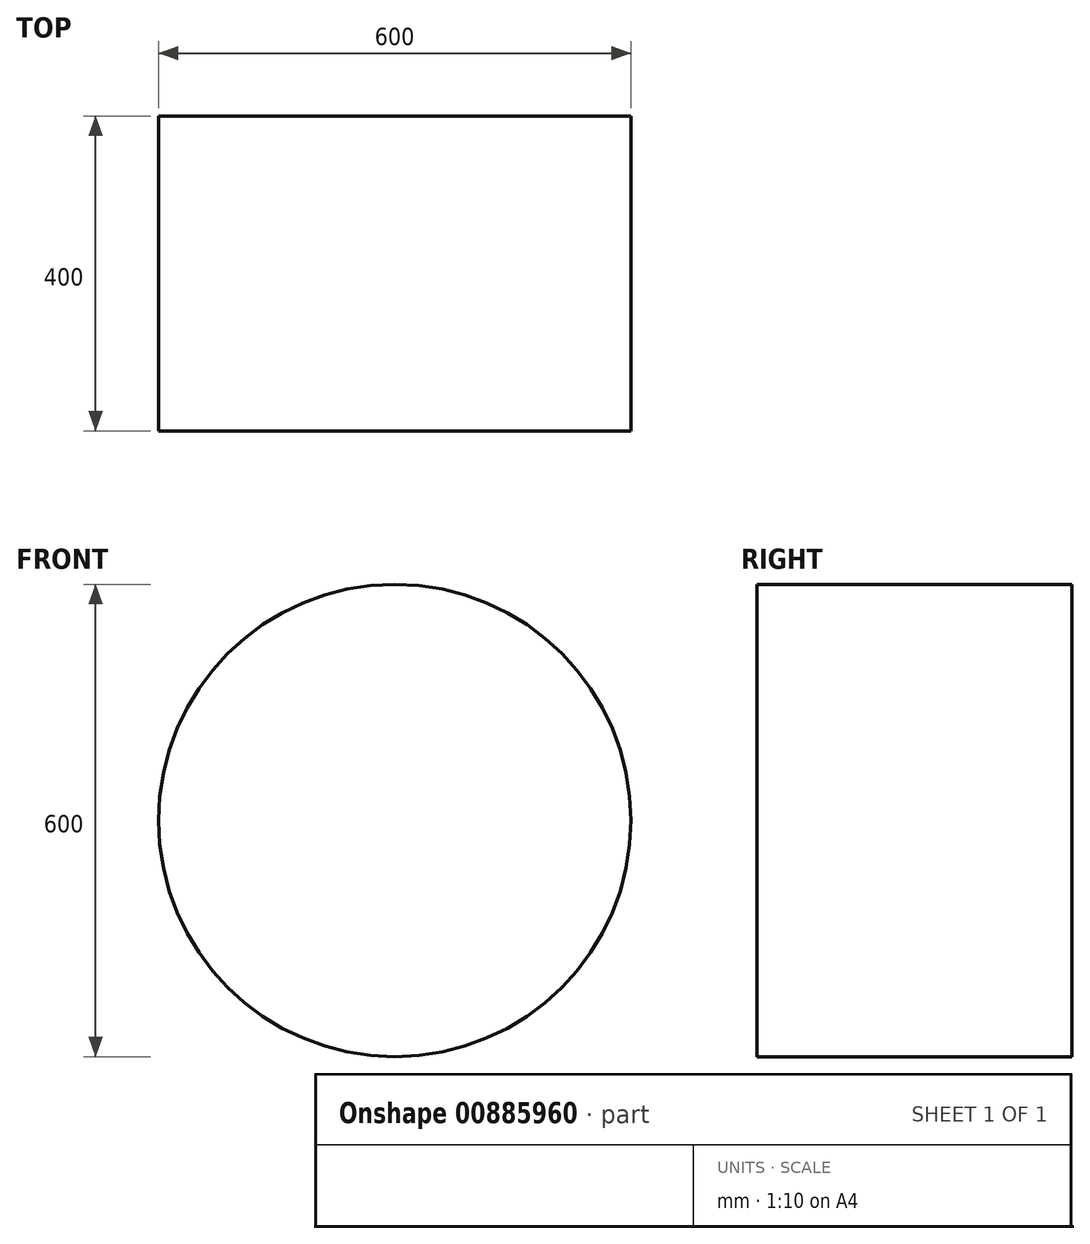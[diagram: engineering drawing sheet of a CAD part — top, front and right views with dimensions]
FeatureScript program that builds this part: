
annotation { "Feature Type Name" : "Feature", "Feature Type Description" : "" }
export const myFeature = defineFeature(function(context is Context, id is Id, definition is map)
    precondition{}
    {
        {
            var Q0;
            Q0=qCreatedBy(makeId("Front.planeOp"),FACE);
            var sketch = newSketch(context, id + "F0", { "sketchPlane" : qUnion([Q0])});
            skCircle(sketch, "E0", {"center": v(0, 0) * mm, "radius": 300 * mm});
            skSolve(sketch);
        }
        {
            var Q0;
            Q0 = qSketchRegion(id + "F0", true);
            var sketch = newSketch(context, id + "F1", { "sketchPlane" : qUnion([Q0])});
            skSolve(sketch);
        }
        {
            var Q0;
            Q0=makeQuery(id+"F1.imprint","IMPRINT",FACE,{"disambiguationData":[TD([[makeQuery(id+"F1.imprint","IMPRINT",EDGE,{"derivedFrom":makeQuery(id+"F0.imprint","IMPRINT",EDGE,{"derivedFrom":sQuery(id+"F0.wireOp",EDGE,"E0")})}),1.0]])]});
            extrude(context, id + "F2", {"entities" : qUnion([Q0]), "depth" : 400 * mm, "offsetDistance" : 25 * mm});
        }
    });
